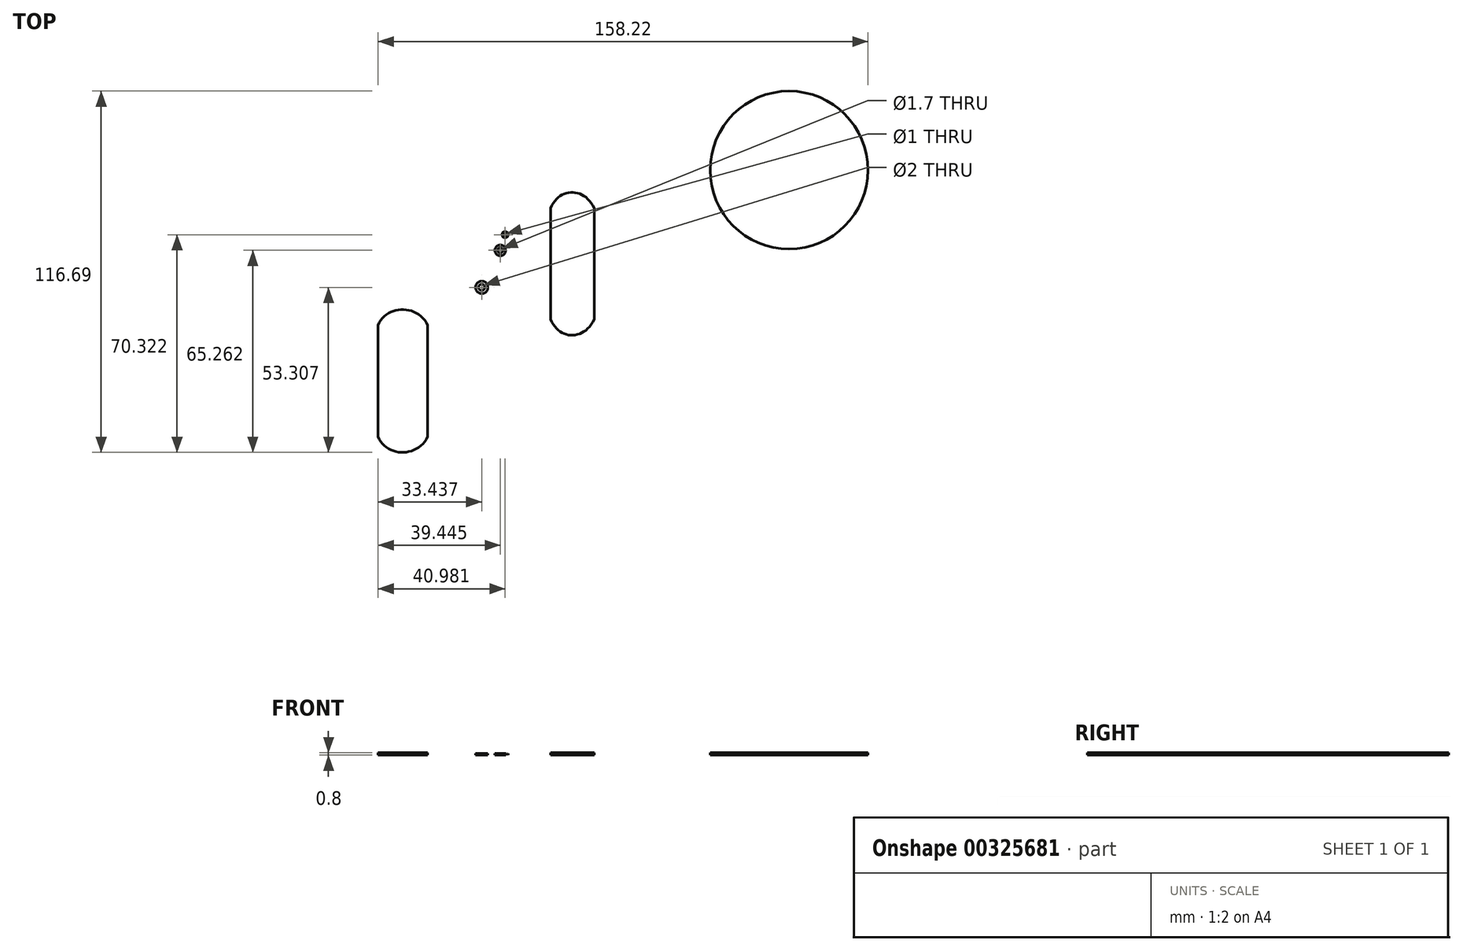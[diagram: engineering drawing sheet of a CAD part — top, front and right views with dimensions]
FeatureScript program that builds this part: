
annotation { "Feature Type Name" : "Feature", "Feature Type Description" : "" }
export const myFeature = defineFeature(function(context is Context, id is Id, definition is map)
    precondition{}
    {
        {
            var Q0;
            Q0=qCreatedBy(makeId("Top.planeOp"),FACE);
            var sketch = newSketch(context, id + "F0", { "sketchPlane" : qUnion([Q0])});
            skLineSegment(sketch, "E0.bottom", {"start": v(-7, 18) * mm, "end": v(7, 18) * mm, "construction": true});
            skLineSegment(sketch, "E0.left", {"start": v(-7, 18) * mm, "end": v(-7, 0) * mm});
            skLineSegment(sketch, "E0.right", {"start": v(7, 18) * mm, "end": v(7, 0) * mm});
            skPoint(sketch, "E0.middle", {"position": v(0, 0) * mm});
            skFitSpline(sketch, "E1", {"points": [v(-7, 18) * mm, v(7, 18) * mm], "startDerivative": vector(7.9, 20.01) * mm, "endDerivative": vector(9.7, -20.55) * mm});
            skLineSegment(sketch, "E2", {"start": v(7, 0) * mm, "end": v(-7, 0) * mm, "construction": true});
            skLineSegment(sketch, "E3.MirrorCS", {"start": v(7, -18) * mm, "end": v(7, 0) * mm});
            skFitSpline(sketch, "E4.MirrorCS", {"points": [v(-7, -18) * mm, v(7, -18) * mm], "startDerivative": vector(7.9, -20.01) * mm, "endDerivative": vector(9.7, 20.55) * mm});
            skLineSegment(sketch, "E5.MirrorCS", {"start": v(-7, -18) * mm, "end": v(-7, 0) * mm});
            skCircle(sketch, "E6", {"center": v(-21.79, 9.4) * mm, "radius": 1 * mm});
            skCircle(sketch, "E7", {"center": v(-23.32, 4.34) * mm, "radius": 1.75 * mm});
            skCircle(sketch, "E8", {"center": v(-21.79, 9.4) * mm, "radius": 0.5 * mm});
            skCircle(sketch, "E9", {"center": v(-23.32, 4.34) * mm, "radius": 0.85 * mm});
            skCircle(sketch, "E10", {"center": v(-29.33, -7.61) * mm, "radius": 2 * mm});
            skCircle(sketch, "E11", {"center": v(-29.33, -7.61) * mm, "radius": 1 * mm});
            skLineSegment(sketch, "E12.bottom", {"start": v(-62.77, -19.85) * mm, "end": v(-46.77, -19.85) * mm, "construction": true});
            skLineSegment(sketch, "E12.left", {"start": v(-62.77, -19.85) * mm, "end": v(-62.77, -37.85) * mm});
            skLineSegment(sketch, "E12.right", {"start": v(-46.77, -19.85) * mm, "end": v(-46.77, -37.85) * mm});
            skPoint(sketch, "E12.middle", {"position": v(-54.77, -37.85) * mm});
            skFitSpline(sketch, "E13", {"points": [v(-62.77, -19.85) * mm, v(-46.77, -19.85) * mm], "startDerivative": vector(7.9, 20.01) * mm, "endDerivative": vector(9.7, -20.55) * mm});
            skLineSegment(sketch, "E14", {"start": v(-46.77, -37.85) * mm, "end": v(-62.77, -37.85) * mm, "construction": true});
            skLineSegment(sketch, "E15.MirrorCS", {"start": v(-46.77, -55.85) * mm, "end": v(-46.77, -37.85) * mm});
            skFitSpline(sketch, "E16.MirrorCS", {"points": [v(-62.77, -55.85) * mm, v(-46.77, -55.85) * mm], "startDerivative": vector(7.9, -20.01) * mm, "endDerivative": vector(9.7, 20.55) * mm});
            skLineSegment(sketch, "E17.MirrorCS", {"start": v(-62.77, -55.85) * mm, "end": v(-62.77, -37.85) * mm});
            skCircle(sketch, "E18", {"center": v(69.95, 30.27) * mm, "radius": 25.5 * mm});
            skSolve(sketch);
        }
        {
            var Q0;
            Q0=makeQuery(id+"F0.imprint","IMPRINT",FACE,{"disambiguationData":[TD([[makeQuery(id+"F0.imprint","IMPRINT",EDGE,{"derivedFrom":sQuery(id+"F0.wireOp",EDGE,"E0.left")}),1.0]])]});
            var Q1;
            Q1=makeQuery(id+"F0.imprint","IMPRINT",FACE,{"disambiguationData":[TD([[makeQuery(id+"F0.imprint","IMPRINT",EDGE,{"derivedFrom":sQuery(id+"F0.wireOp",EDGE,"E12.left")}),1.0]])]});
            var Q2;
            Q2=makeQuery(id+"F0.imprint","IMPRINT",FACE,{"disambiguationData":[TD([[makeQuery(id+"F0.imprint","IMPRINT",EDGE,{"derivedFrom":sQuery(id+"F0.wireOp",EDGE,"E18")}),1.0]])]});
            extrude(context, id + "F1", {"entities" : qUnion([Q0, Q1, Q2]), "depth" : .8 * mm});
        }
        {
            var Q0;
            Q0=makeQuery(id+"F0.imprint","IMPRINT",FACE,{"disambiguationData":[TD([[makeQuery(id+"F0.imprint","IMPRINT",EDGE,{"derivedFrom":sQuery(id+"F0.wireOp",EDGE,"E6")}),1.0]])]});
            var Q1;
            Q1=makeQuery(id+"F0.imprint","IMPRINT",FACE,{"disambiguationData":[TD([[makeQuery(id+"F0.imprint","IMPRINT",EDGE,{"derivedFrom":sQuery(id+"F0.wireOp",EDGE,"E7")}),1.0]])]});
            var Q2;
            Q2=makeQuery(id+"F0.imprint","IMPRINT",FACE,{"disambiguationData":[TD([[makeQuery(id+"F0.imprint","IMPRINT",EDGE,{"derivedFrom":sQuery(id+"F0.wireOp",EDGE,"E10")}),1.0]])]});
            extrude(context, id + "F2", {"entities" : qUnion([Q0, Q1, Q2]), "depth" : .5 * mm});
        }
    });
